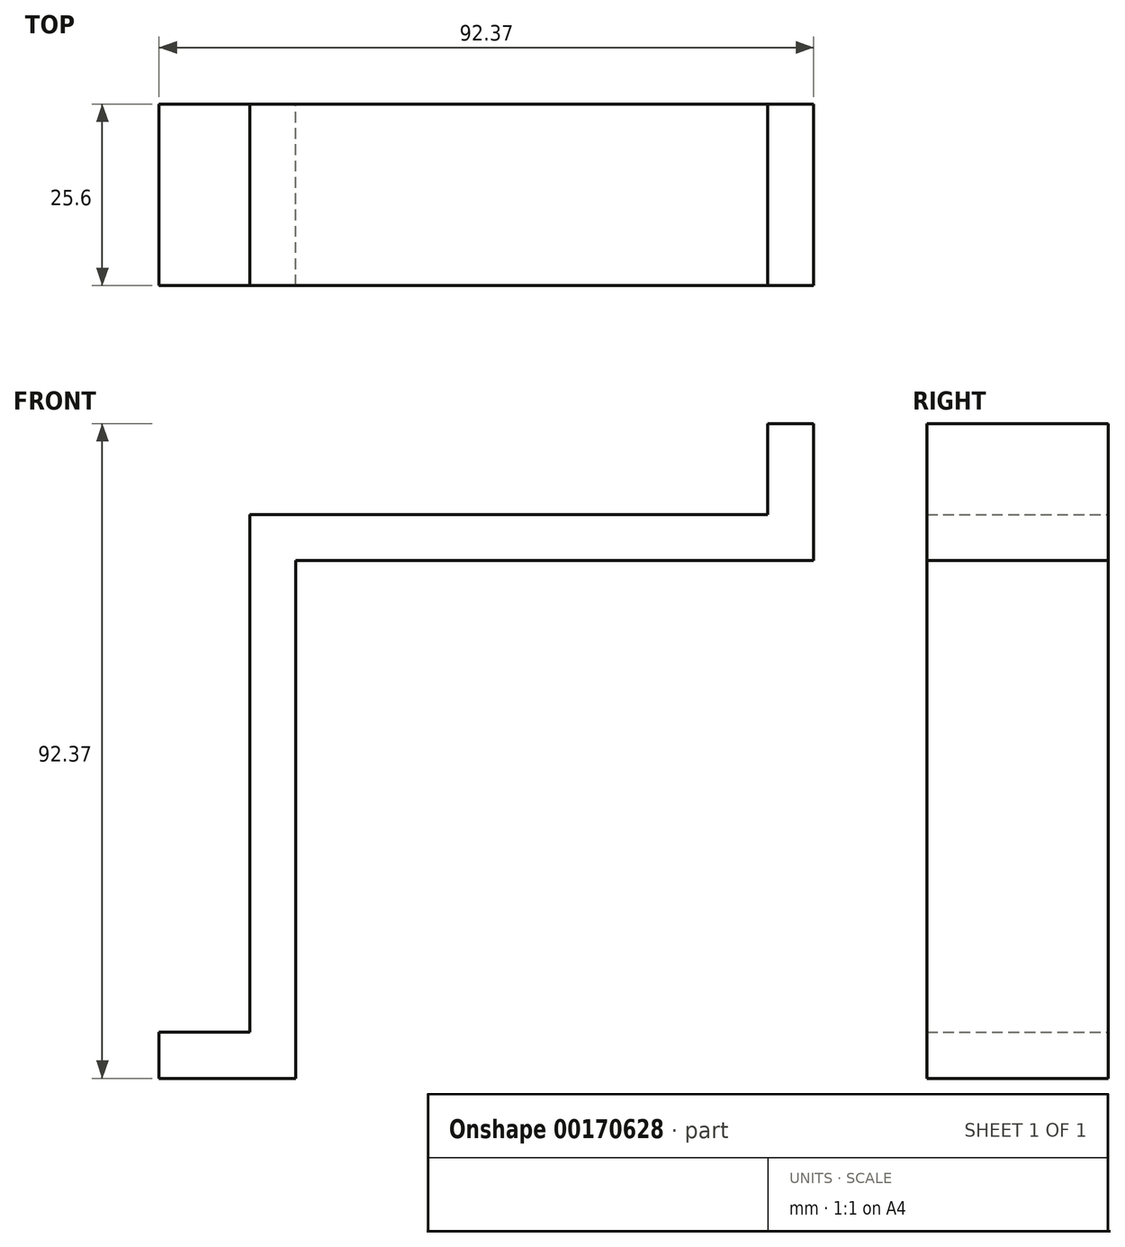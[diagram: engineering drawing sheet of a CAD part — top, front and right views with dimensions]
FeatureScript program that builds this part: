
annotation { "Feature Type Name" : "Feature", "Feature Type Description" : "" }
export const myFeature = defineFeature(function(context is Context, id is Id, definition is map)
    precondition{}
    {
        {
            var Q0;
            Q0=qCreatedBy(makeId("Front.planeOp"),FACE);
            var sketch = newSketch(context, id + "F0", { "sketchPlane" : qUnion([Q0])});
            skLineSegment(sketch, "E0", {"start": v(0, 0) * mm, "end": v(-73.07, 0) * mm});
            skLineSegment(sketch, "E1", {"start": v(-73.07, 0) * mm, "end": v(-73.07, -73.07) * mm});
            skLineSegment(sketch, "E2", {"start": v(-73.07, -73.07) * mm, "end": v(-92.37, -73.07) * mm});
            skLineSegment(sketch, "E3", {"start": v(-92.37, -73.07) * mm, "end": v(-92.37, -66.57) * mm});
            skLineSegment(sketch, "E4", {"start": v(-79.57, -66.57) * mm, "end": v(-79.57, 0) * mm});
            skLineSegment(sketch, "E5", {"start": v(-79.57, 0) * mm, "end": v(-79.57, 6.5) * mm});
            skLineSegment(sketch, "E6", {"start": v(-92.37, -66.57) * mm, "end": v(-79.57, -66.57) * mm});
            skLineSegment(sketch, "E7", {"start": v(0, 0) * mm, "end": v(0, 19.3) * mm});
            skLineSegment(sketch, "E8", {"start": v(0, 19.3) * mm, "end": v(-6.5, 19.3) * mm});
            skLineSegment(sketch, "E9", {"start": v(-6.5, 19.3) * mm, "end": v(-6.5, 6.5) * mm});
            skLineSegment(sketch, "E10", {"start": v(-6.5, 6.5) * mm, "end": v(-79.57, 6.5) * mm});
            skSolve(sketch);
        }
        {
            var Q0;
            Q0=makeQuery(id+"F0.imprint","IMPRINT",FACE,{"disambiguationData":[TD([[makeQuery(id+"F0.imprint","IMPRINT",EDGE,{"derivedFrom":sQuery(id+"F0.wireOp",EDGE,"E0")}),-1.0]])]});
            extrude(context, id + "F1", {"entities" : qUnion([Q0]), "depth" : 25.6 * mm});
        }
    });
